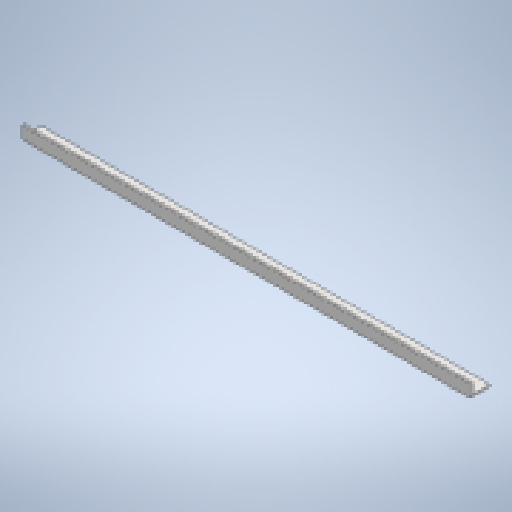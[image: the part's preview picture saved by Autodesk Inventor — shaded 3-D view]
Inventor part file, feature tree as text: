
AUTODESK INVENTOR PART (.ipt)
format: ipt  version: 2023 (Build 270158000, 158)  size: 139,776 bytes
history: native  units: in
note: dims shown in document units (in); Inventor stores cm internally (conversion verified against a paired STEP export)
features: extrude x1, sketch x1
ambient origin geometry x8: Origin, YZ Plane, XZ Plane, XY Plane, X Axis, Y Axis, Z Axis, Center Point
bodies: Solid1 (feature_tree)
feature tree (2):
  extrude  "Extrusion1"  Depth=2.3333in
  sketch  "Sketch1"  dims[d0=1.5in d1=2.3333in d2=0.25in d3=0.25in d4=54.0in d5=0.0in]
